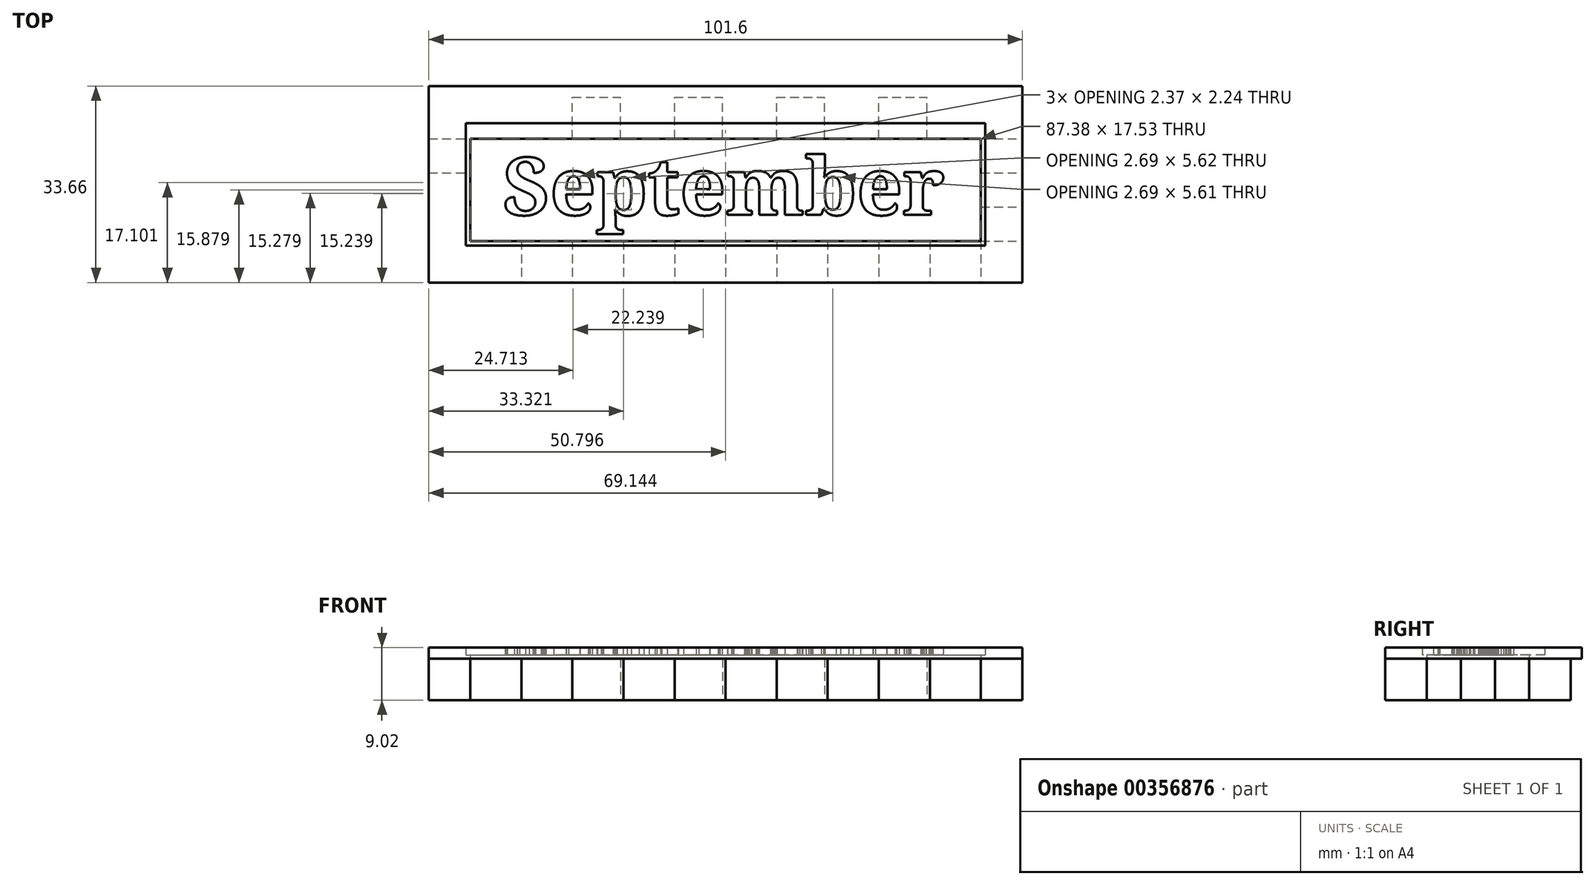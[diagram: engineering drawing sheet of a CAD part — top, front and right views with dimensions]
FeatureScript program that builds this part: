
annotation { "Feature Type Name" : "Feature", "Feature Type Description" : "" }
export const myFeature = defineFeature(function(context is Context, id is Id, definition is map)
    precondition{}
    {
        {
            var Q0;
            Q0=qCreatedBy(makeId("Top.planeOp"),FACE);
            var sketch = newSketch(context, id + "F0", { "sketchPlane" : qUnion([Q0])});
            skLineSegment(sketch, "E0.bottom", {"start": v(-52.12, 11.37) * mm, "end": v(49.48, 11.37) * mm});
            skLineSegment(sketch, "E0.top", {"start": v(-52.12, -20.38) * mm, "end": v(49.48, -20.38) * mm});
            skLineSegment(sketch, "E0.left", {"start": v(-52.12, 11.37) * mm, "end": v(-52.12, -20.38) * mm});
            skLineSegment(sketch, "E0.right", {"start": v(49.48, 11.37) * mm, "end": v(49.48, -20.38) * mm});
            skLineSegment(sketch, "E1.bottom", {"start": v(-52.12, 11.37) * mm, "end": v(-45.01, 11.37) * mm});
            skLineSegment(sketch, "E1.top", {"start": v(-52.12, 4.26) * mm, "end": v(-45.01, 4.26) * mm});
            skLineSegment(sketch, "E1.left", {"start": v(-52.12, 11.37) * mm, "end": v(-52.12, 4.26) * mm});
            skLineSegment(sketch, "E1.right", {"start": v(-45.01, 11.37) * mm, "end": v(-45.01, 4.26) * mm});
            skLineSegment(sketch, "E2.bottom", {"start": v(-45.01, 11.37) * mm, "end": v(-36.78, 11.37) * mm});
            skLineSegment(sketch, "E2.top", {"start": v(-45.01, 4.26) * mm, "end": v(-36.78, 4.26) * mm});
            skLineSegment(sketch, "E2.right", {"start": v(-36.78, 11.37) * mm, "end": v(-36.78, 4.26) * mm});
            skLineSegment(sketch, "E3.bottom", {"start": v(-36.78, 4.26) * mm, "end": v(-27.54, 4.26) * mm});
            skLineSegment(sketch, "E3.top", {"start": v(-36.78, 11.37) * mm, "end": v(-27.54, 11.37) * mm});
            skLineSegment(sketch, "E3.left", {"start": v(-36.78, 4.26) * mm, "end": v(-36.78, 11.37) * mm});
            skLineSegment(sketch, "E3.right", {"start": v(-27.54, 4.26) * mm, "end": v(-27.54, 11.37) * mm});
            skLineSegment(sketch, "E4.bottom", {"start": v(-27.54, 4.26) * mm, "end": v(-19.3, 4.26) * mm});
            skLineSegment(sketch, "E4.top", {"start": v(-27.54, 11.37) * mm, "end": v(-19.3, 11.37) * mm});
            skLineSegment(sketch, "E4.right", {"start": v(-19.3, 4.26) * mm, "end": v(-19.3, 11.37) * mm});
            skLineSegment(sketch, "E5.bottom", {"start": v(-19.3, 4.26) * mm, "end": v(-10.06, 4.26) * mm});
            skLineSegment(sketch, "E5.top", {"start": v(-19.3, 11.37) * mm, "end": v(-10.06, 11.37) * mm});
            skLineSegment(sketch, "E5.right", {"start": v(-10.06, 4.26) * mm, "end": v(-10.06, 11.37) * mm});
            skLineSegment(sketch, "E6.bottom", {"start": v(-10.06, 4.26) * mm, "end": v(-10.06, 4.26) * mm});
            skLineSegment(sketch, "E6.top", {"start": v(-10.06, 11.37) * mm, "end": v(-10.06, 11.37) * mm});
            skLineSegment(sketch, "E7.bottom", {"start": v(-10.06, 4.26) * mm, "end": v(-1.83, 4.26) * mm});
            skLineSegment(sketch, "E7.top", {"start": v(-10.06, 11.37) * mm, "end": v(-1.83, 11.37) * mm});
            skLineSegment(sketch, "E7.right", {"start": v(-1.83, 4.26) * mm, "end": v(-1.83, 11.37) * mm});
            skLineSegment(sketch, "E8.bottom", {"start": v(-1.83, 4.26) * mm, "end": v(7.41, 4.26) * mm});
            skLineSegment(sketch, "E8.top", {"start": v(-1.83, 11.37) * mm, "end": v(7.41, 11.37) * mm});
            skLineSegment(sketch, "E8.right", {"start": v(7.41, 4.26) * mm, "end": v(7.41, 11.37) * mm});
            skLineSegment(sketch, "E9.bottom", {"start": v(7.41, 4.26) * mm, "end": v(15.64, 4.26) * mm});
            skLineSegment(sketch, "E9.top", {"start": v(7.41, 11.37) * mm, "end": v(15.64, 11.37) * mm});
            skLineSegment(sketch, "E9.right", {"start": v(15.64, 4.26) * mm, "end": v(15.64, 11.37) * mm});
            skLineSegment(sketch, "E10.bottom", {"start": v(15.64, 4.26) * mm, "end": v(24.89, 4.26) * mm});
            skLineSegment(sketch, "E10.top", {"start": v(15.64, 11.37) * mm, "end": v(24.89, 11.37) * mm});
            skLineSegment(sketch, "E10.right", {"start": v(24.89, 4.26) * mm, "end": v(24.89, 11.37) * mm});
            skLineSegment(sketch, "E11.bottom", {"start": v(24.89, 4.26) * mm, "end": v(24.89, 4.26) * mm});
            skLineSegment(sketch, "E11.top", {"start": v(24.89, 11.37) * mm, "end": v(24.89, 11.37) * mm});
            skLineSegment(sketch, "E12.bottom", {"start": v(24.89, 4.26) * mm, "end": v(33.12, 4.26) * mm});
            skLineSegment(sketch, "E12.top", {"start": v(24.89, 11.37) * mm, "end": v(33.12, 11.37) * mm});
            skLineSegment(sketch, "E12.right", {"start": v(33.12, 4.26) * mm, "end": v(33.12, 11.37) * mm});
            skLineSegment(sketch, "E13.bottom", {"start": v(33.12, 4.26) * mm, "end": v(42.36, 4.26) * mm});
            skLineSegment(sketch, "E13.top", {"start": v(33.12, 11.37) * mm, "end": v(42.36, 11.37) * mm});
            skLineSegment(sketch, "E13.right", {"start": v(42.36, 4.26) * mm, "end": v(42.36, 11.37) * mm});
            skLineSegment(sketch, "E14.bottom", {"start": v(42.36, 4.26) * mm, "end": v(49.48, 4.26) * mm});
            skLineSegment(sketch, "E14.top", {"start": v(42.36, 11.37) * mm, "end": v(49.48, 11.37) * mm});
            skLineSegment(sketch, "E14.right", {"start": v(49.48, 4.26) * mm, "end": v(49.48, 11.37) * mm});
            skLineSegment(sketch, "E15.bottom", {"start": v(-52.12, -20.38) * mm, "end": v(-45.01, -20.38) * mm});
            skLineSegment(sketch, "E15.top", {"start": v(-52.12, -13.26) * mm, "end": v(-45.01, -13.26) * mm});
            skLineSegment(sketch, "E15.left", {"start": v(-52.12, -20.38) * mm, "end": v(-52.12, -13.26) * mm});
            skLineSegment(sketch, "E15.right", {"start": v(-45.01, -20.38) * mm, "end": v(-45.01, -13.26) * mm});
            skLineSegment(sketch, "E16.bottom", {"start": v(-45.01, -13.26) * mm, "end": v(-45.01, -13.26) * mm});
            skLineSegment(sketch, "E16.top", {"start": v(-45.01, -20.38) * mm, "end": v(-45.01, -20.38) * mm});
            skLineSegment(sketch, "E16.left", {"start": v(-45.01, -13.26) * mm, "end": v(-45.01, -20.38) * mm});
            skLineSegment(sketch, "E16.right", {"start": v(-45.01, -13.26) * mm, "end": v(-45.01, -20.38) * mm});
            skLineSegment(sketch, "E17.bottom", {"start": v(-45.01, -13.26) * mm, "end": v(-36.27, -13.26) * mm});
            skLineSegment(sketch, "E17.top", {"start": v(-45.01, -20.38) * mm, "end": v(-36.27, -20.38) * mm});
            skLineSegment(sketch, "E17.right", {"start": v(-36.27, -13.26) * mm, "end": v(-36.27, -20.38) * mm});
            skLineSegment(sketch, "E18.bottom", {"start": v(-36.27, -13.26) * mm, "end": v(-36.27, -13.26) * mm});
            skLineSegment(sketch, "E18.top", {"start": v(-36.27, -20.38) * mm, "end": v(-36.27, -20.38) * mm});
            skLineSegment(sketch, "E19.bottom", {"start": v(-36.27, -13.26) * mm, "end": v(-27.54, -13.26) * mm});
            skLineSegment(sketch, "E19.top", {"start": v(-36.27, -20.38) * mm, "end": v(-27.54, -20.38) * mm});
            skLineSegment(sketch, "E19.right", {"start": v(-27.54, -13.26) * mm, "end": v(-27.54, -20.38) * mm});
            skLineSegment(sketch, "E20.bottom", {"start": v(-27.54, -13.26) * mm, "end": v(-18.8, -13.26) * mm});
            skLineSegment(sketch, "E20.top", {"start": v(-27.54, -20.38) * mm, "end": v(-18.8, -20.38) * mm});
            skLineSegment(sketch, "E20.right", {"start": v(-18.8, -13.26) * mm, "end": v(-18.8, -20.38) * mm});
            skLineSegment(sketch, "E21.bottom", {"start": v(-18.8, -13.26) * mm, "end": v(-10.06, -13.26) * mm});
            skLineSegment(sketch, "E21.top", {"start": v(-18.8, -20.38) * mm, "end": v(-10.06, -20.38) * mm});
            skLineSegment(sketch, "E21.right", {"start": v(-10.06, -13.26) * mm, "end": v(-10.06, -20.38) * mm});
            skLineSegment(sketch, "E22.bottom", {"start": v(-10.06, -13.26) * mm, "end": v(-1.32, -13.26) * mm});
            skLineSegment(sketch, "E22.top", {"start": v(-10.06, -20.38) * mm, "end": v(-1.32, -20.38) * mm});
            skLineSegment(sketch, "E22.right", {"start": v(-1.32, -13.26) * mm, "end": v(-1.32, -20.38) * mm});
            skLineSegment(sketch, "E23.bottom", {"start": v(-1.32, -13.26) * mm, "end": v(7.41, -13.26) * mm});
            skLineSegment(sketch, "E23.top", {"start": v(-1.32, -20.38) * mm, "end": v(7.41, -20.38) * mm});
            skLineSegment(sketch, "E23.right", {"start": v(7.41, -13.26) * mm, "end": v(7.41, -20.38) * mm});
            skLineSegment(sketch, "E24.bottom", {"start": v(7.41, -13.26) * mm, "end": v(16.15, -13.26) * mm});
            skLineSegment(sketch, "E24.top", {"start": v(7.41, -20.38) * mm, "end": v(16.15, -20.38) * mm});
            skLineSegment(sketch, "E24.right", {"start": v(16.15, -13.26) * mm, "end": v(16.15, -20.38) * mm});
            skLineSegment(sketch, "E25.bottom", {"start": v(16.15, -13.26) * mm, "end": v(24.89, -13.26) * mm});
            skLineSegment(sketch, "E25.top", {"start": v(16.15, -20.38) * mm, "end": v(24.89, -20.38) * mm});
            skLineSegment(sketch, "E25.right", {"start": v(24.89, -13.26) * mm, "end": v(24.89, -20.38) * mm});
            skLineSegment(sketch, "E26.bottom", {"start": v(24.89, -13.26) * mm, "end": v(33.63, -13.26) * mm});
            skLineSegment(sketch, "E26.top", {"start": v(24.89, -20.38) * mm, "end": v(33.63, -20.38) * mm});
            skLineSegment(sketch, "E26.right", {"start": v(33.63, -13.26) * mm, "end": v(33.63, -20.38) * mm});
            skLineSegment(sketch, "E27.bottom", {"start": v(33.63, -13.26) * mm, "end": v(42.36, -13.26) * mm});
            skLineSegment(sketch, "E27.top", {"start": v(33.63, -20.38) * mm, "end": v(42.36, -20.38) * mm});
            skLineSegment(sketch, "E27.right", {"start": v(42.36, -13.26) * mm, "end": v(42.36, -20.38) * mm});
            skLineSegment(sketch, "E28.bottom", {"start": v(42.36, -13.26) * mm, "end": v(49.48, -13.26) * mm});
            skLineSegment(sketch, "E28.top", {"start": v(42.36, -20.38) * mm, "end": v(49.48, -20.38) * mm});
            skLineSegment(sketch, "E28.right", {"start": v(49.48, -13.26) * mm, "end": v(49.48, -20.38) * mm});
            skLineSegment(sketch, "E29.top", {"start": v(-52.12, -1.58) * mm, "end": v(-45.01, -1.58) * mm});
            skLineSegment(sketch, "E29.left", {"start": v(-52.12, 4.26) * mm, "end": v(-52.12, -1.58) * mm});
            skLineSegment(sketch, "E29.right", {"start": v(-45.01, 4.26) * mm, "end": v(-45.01, -1.58) * mm});
            skLineSegment(sketch, "E30.top", {"start": v(-52.12, -7.42) * mm, "end": v(-45.01, -7.42) * mm});
            skLineSegment(sketch, "E30.left", {"start": v(-52.12, -1.58) * mm, "end": v(-52.12, -7.42) * mm});
            skLineSegment(sketch, "E30.right", {"start": v(-45.01, -1.58) * mm, "end": v(-45.01, -7.42) * mm});
            skLineSegment(sketch, "E31.bottom", {"start": v(-45.01, -7.42) * mm, "end": v(-52.12, -7.42) * mm});
            skLineSegment(sketch, "E31.top", {"start": v(-45.01, -13.26) * mm, "end": v(-52.12, -13.26) * mm});
            skLineSegment(sketch, "E31.left", {"start": v(-45.01, -7.42) * mm, "end": v(-45.01, -13.26) * mm});
            skLineSegment(sketch, "E31.right", {"start": v(-52.12, -7.42) * mm, "end": v(-52.12, -13.26) * mm});
            skLineSegment(sketch, "E32.top", {"start": v(42.36, -1.58) * mm, "end": v(49.48, -1.58) * mm});
            skLineSegment(sketch, "E32.left", {"start": v(42.36, 4.26) * mm, "end": v(42.36, -1.58) * mm});
            skLineSegment(sketch, "E32.right", {"start": v(49.48, 4.26) * mm, "end": v(49.48, -1.58) * mm});
            skLineSegment(sketch, "E33.top", {"start": v(42.36, -7.42) * mm, "end": v(49.48, -7.42) * mm});
            skLineSegment(sketch, "E33.left", {"start": v(42.36, -1.58) * mm, "end": v(42.36, -7.42) * mm});
            skLineSegment(sketch, "E33.right", {"start": v(49.48, -1.58) * mm, "end": v(49.48, -7.42) * mm});
            skLineSegment(sketch, "E34.left", {"start": v(42.36, -7.42) * mm, "end": v(42.36, -13.26) * mm});
            skLineSegment(sketch, "E34.right", {"start": v(49.48, -7.42) * mm, "end": v(49.48, -13.26) * mm});
            skSolve(sketch);
        }
        {
            var Q0;
            Q0=makeQuery(id+"F0.imprint","IMPRINT",FACE,{"disambiguationData":[TD([[makeQuery(id+"F0.imprint","IMPRINT",EDGE,{"derivedFrom":sQuery(id+"F0.wireOp",EDGE,"E2.top")}),-1.0]])]});
            var Q1;
            Q1=makeQuery(id+"F0.imprint","IMPRINT",FACE,{"disambiguationData":[TD([[makeQuery(id+"F0.imprint","IMPRINT",EDGE,{"derivedFrom":sQuery(id+"F0.wireOp",EDGE,"E2.bottom")}),-1.0]])]});
            var Q2;
            Q2=makeQuery(id+"F0.imprint","IMPRINT",FACE,{"disambiguationData":[TD([[makeQuery(id+"F0.imprint","IMPRINT",EDGE,{"derivedFrom":sQuery(id+"F0.wireOp",EDGE,"E4.bottom")}),1.0]])]});
            var Q3;
            Q3=makeQuery(id+"F0.imprint","IMPRINT",FACE,{"disambiguationData":[TD([[makeQuery(id+"F0.imprint","IMPRINT",EDGE,{"derivedFrom":sQuery(id+"F0.wireOp",EDGE,"E7.bottom")}),1.0]])]});
            var Q4;
            Q4=makeQuery(id+"F0.imprint","IMPRINT",FACE,{"disambiguationData":[TD([[makeQuery(id+"F0.imprint","IMPRINT",EDGE,{"derivedFrom":sQuery(id+"F0.wireOp",EDGE,"E9.bottom")}),1.0]])]});
            var Q5;
            Q5=makeQuery(id+"F0.imprint","IMPRINT",FACE,{"disambiguationData":[TD([[makeQuery(id+"F0.imprint","IMPRINT",EDGE,{"derivedFrom":sQuery(id+"F0.wireOp",EDGE,"E12.bottom")}),1.0]])]});
            var Q6;
            Q6=makeQuery(id+"F0.imprint","IMPRINT",FACE,{"disambiguationData":[TD([[makeQuery(id+"F0.imprint","IMPRINT",EDGE,{"derivedFrom":sQuery(id+"F0.wireOp",EDGE,"E14.bottom")}),-1.0]])]});
            var Q7;
            Q7=makeQuery(id+"F0.imprint","IMPRINT",FACE,{"disambiguationData":[TD([[makeQuery(id+"F0.imprint","IMPRINT",EDGE,{"derivedFrom":sQuery(id+"F0.wireOp",EDGE,"E33.top")}),-1.0]])]});
            var Q8;
            Q8=makeQuery(id+"F0.imprint","IMPRINT",FACE,{"disambiguationData":[TD([[makeQuery(id+"F0.imprint","IMPRINT",EDGE,{"derivedFrom":sQuery(id+"F0.wireOp",EDGE,"E27.bottom")}),-1.0]])]});
            var Q9;
            Q9=makeQuery(id+"F0.imprint","IMPRINT",FACE,{"disambiguationData":[TD([[makeQuery(id+"F0.imprint","IMPRINT",EDGE,{"derivedFrom":sQuery(id+"F0.wireOp",EDGE,"E25.bottom")}),-1.0]])]});
            var Q10;
            Q10=makeQuery(id+"F0.imprint","IMPRINT",FACE,{"disambiguationData":[TD([[makeQuery(id+"F0.imprint","IMPRINT",EDGE,{"derivedFrom":sQuery(id+"F0.wireOp",EDGE,"E23.bottom")}),-1.0]])]});
            var Q11;
            Q11=makeQuery(id+"F0.imprint","IMPRINT",FACE,{"disambiguationData":[TD([[makeQuery(id+"F0.imprint","IMPRINT",EDGE,{"derivedFrom":sQuery(id+"F0.wireOp",EDGE,"E21.bottom")}),-1.0]])]});
            var Q12;
            Q12=makeQuery(id+"F0.imprint","IMPRINT",FACE,{"disambiguationData":[TD([[makeQuery(id+"F0.imprint","IMPRINT",EDGE,{"derivedFrom":sQuery(id+"F0.wireOp",EDGE,"E19.bottom")}),-1.0]])]});
            var Q13;
            Q13=makeQuery(id+"F0.imprint","IMPRINT",FACE,{"disambiguationData":[TD([[makeQuery(id+"F0.imprint","IMPRINT",EDGE,{"derivedFrom":sQuery(id+"F0.wireOp",EDGE,"E31.bottom")}),1.0]])]});
            var Q14;
            Q14=makeQuery(id+"F0.imprint","IMPRINT",FACE,{"disambiguationData":[TD([[makeQuery(id+"F0.imprint","IMPRINT",EDGE,{"derivedFrom":sQuery(id+"F0.wireOp",EDGE,"E1.top")}),-1.0]])]});
            extrude(context, id + "F1", {"entities" : qUnion([Q0, Q1, Q2, Q3, Q4, Q5, Q6, Q7, Q8, Q9, Q10, Q11, Q12, Q13, Q14]), "depth" : 7.11 * mm});
        }
        {
            var Q0;
            Q0=makeQuery(id+"F1.opExtrude","CAP_FACE",FACE,{"disambiguationData":[OSD([sQuery(id+"F0.wireOp",EDGE,"E2.bottom"),sQuery(id+"F0.wireOp",EDGE,"E1.right"),sQuery(id+"F0.wireOp",EDGE,"E3.bottom"),sQuery(id+"F0.wireOp",EDGE,"E3.left"),sQuery(id+"F0.wireOp",EDGE,"E4.top"),sQuery(id+"F0.wireOp",EDGE,"E3.right"),sQuery(id+"F0.wireOp",EDGE,"E5.bottom"),sQuery(id+"F0.wireOp",EDGE,"E4.right"),sQuery(id+"F0.wireOp",EDGE,"E6.top"),sQuery(id+"F0.wireOp",EDGE,"E5.right"),sQuery(id+"F0.wireOp",EDGE,"E7.bottom"),sQuery(id+"F0.wireOp",EDGE,"E5.right"),sQuery(id+"F0.wireOp",EDGE,"E8.top"),sQuery(id+"F0.wireOp",EDGE,"E7.right"),sQuery(id+"F0.wireOp",EDGE,"E9.bottom"),sQuery(id+"F0.wireOp",EDGE,"E8.right"),sQuery(id+"F0.wireOp",EDGE,"E10.top"),sQuery(id+"F0.wireOp",EDGE,"E9.right"),sQuery(id+"F0.wireOp",EDGE,"E11.bottom"),sQuery(id+"F0.wireOp",EDGE,"E10.right"),sQuery(id+"F0.wireOp",EDGE,"E12.top"),sQuery(id+"F0.wireOp",EDGE,"E10.right"),sQuery(id+"F0.wireOp",EDGE,"E13.bottom"),sQuery(id+"F0.wireOp",EDGE,"E12.right"),sQuery(id+"F0.wireOp",EDGE,"E16.bottom"),sQuery(id+"F0.wireOp",EDGE,"E17.top"),sQuery(id+"F0.wireOp",EDGE,"E16.left"),sQuery(id+"F0.wireOp",EDGE,"E18.bottom"),sQuery(id+"F0.wireOp",EDGE,"E17.right"),sQuery(id+"F0.wireOp",EDGE,"E19.top"),sQuery(id+"F0.wireOp",EDGE,"E17.right"),sQuery(id+"F0.wireOp",EDGE,"E20.bottom"),sQuery(id+"F0.wireOp",EDGE,"E19.right"),sQuery(id+"F0.wireOp",EDGE,"E21.top"),sQuery(id+"F0.wireOp",EDGE,"E20.right"),sQuery(id+"F0.wireOp",EDGE,"E22.bottom"),sQuery(id+"F0.wireOp",EDGE,"E21.right"),sQuery(id+"F0.wireOp",EDGE,"E23.top"),sQuery(id+"F0.wireOp",EDGE,"E22.right"),sQuery(id+"F0.wireOp",EDGE,"E24.bottom"),sQuery(id+"F0.wireOp",EDGE,"E23.right"),sQuery(id+"F0.wireOp",EDGE,"E25.top"),sQuery(id+"F0.wireOp",EDGE,"E24.right"),sQuery(id+"F0.wireOp",EDGE,"E26.bottom"),sQuery(id+"F0.wireOp",EDGE,"E25.right"),sQuery(id+"F0.wireOp",EDGE,"E27.top"),sQuery(id+"F0.wireOp",EDGE,"E26.right"),sQuery(id+"F0.wireOp",EDGE,"E27.right"),sQuery(id+"F0.wireOp",EDGE,"E1.top"),sQuery(id+"F0.wireOp",EDGE,"E29.left"),sQuery(id+"F0.wireOp",EDGE,"E29.top"),sQuery(id+"F0.wireOp",EDGE,"E30.right"),sQuery(id+"F0.wireOp",EDGE,"E31.bottom"),sQuery(id+"F0.wireOp",EDGE,"E31.top"),sQuery(id+"F0.wireOp",EDGE,"E31.right"),sQuery(id+"F0.wireOp",EDGE,"E14.bottom"),sQuery(id+"F0.wireOp",EDGE,"E32.right"),sQuery(id+"F0.wireOp",EDGE,"E32.top"),sQuery(id+"F0.wireOp",EDGE,"E33.left"),sQuery(id+"F0.wireOp",EDGE,"E33.top"),sQuery(id+"F0.wireOp",EDGE,"E28.bottom"),sQuery(id+"F0.wireOp",EDGE,"E34.right")])],"isStart":false});
            var sketch = newSketch(context, id + "F2", { "sketchPlane" : qUnion([Q0])});
            skLineSegment(sketch, "E35.bottom", {"start": v(-52.12, -20.38) * mm, "end": v(-45.01, -20.38) * mm});
            skLineSegment(sketch, "E35.top", {"start": v(-52.12, 13.28) * mm, "end": v(-45.01, 13.28) * mm});
            skLineSegment(sketch, "E35.left", {"start": v(-52.12, -20.38) * mm, "end": v(-52.12, 13.28) * mm});
            skLineSegment(sketch, "E35.right", {"start": v(-45.01, -20.38) * mm, "end": v(-45.01, 13.28) * mm});
            skLineSegment(sketch, "E36.bottom", {"start": v(-52.12, -20.38) * mm, "end": v(49.48, -20.38) * mm});
            skLineSegment(sketch, "E36.top", {"start": v(-52.12, -13.26) * mm, "end": v(49.48, -13.26) * mm});
            skLineSegment(sketch, "E36.left", {"start": v(-52.12, -20.38) * mm, "end": v(-52.12, -13.26) * mm});
            skLineSegment(sketch, "E36.right", {"start": v(49.48, -20.38) * mm, "end": v(49.48, -13.26) * mm});
            skPoint(sketch, "E37.oppositeSnap0", {"position": v(42.36, -4.5) * mm});
            skLineSegment(sketch, "E37.bottom", {"start": v(49.48, -20.38) * mm, "end": v(42.36, -20.38) * mm});
            skLineSegment(sketch, "E37.top", {"start": v(49.48, 13.28) * mm, "end": v(42.36, 13.28) * mm});
            skLineSegment(sketch, "E37.left", {"start": v(49.48, -20.38) * mm, "end": v(49.48, 13.28) * mm});
            skLineSegment(sketch, "E37.right", {"start": v(42.36, -20.38) * mm, "end": v(42.36, 13.28) * mm});
            skLineSegment(sketch, "E38.bottom", {"start": v(-52.12, 13.28) * mm, "end": v(49.48, 13.28) * mm});
            skLineSegment(sketch, "E38.top", {"start": v(-52.12, 4.26) * mm, "end": v(49.48, 4.26) * mm});
            skLineSegment(sketch, "E38.left", {"start": v(-52.12, 13.28) * mm, "end": v(-52.12, 4.26) * mm});
            skLineSegment(sketch, "E38.right", {"start": v(49.48, 13.28) * mm, "end": v(49.48, 4.26) * mm});
            skSolve(sketch);
        }
        {
            var Q0;
            Q0=qSketchRegion(id+"F2",true);
            var Q1;
            {var subQ5=sQuery(id+"F2.wireOp",EDGE,"E36.top");var subQ10=sQuery(id+"F2.wireOp",EDGE,"E35.right");var subQ12=makeQuery(id+"F2.imprint","INTERSECT",VERTEX,{"derivedFrom":[makeQuery(id+"F1.opExtrude","CAP_EDGE",EDGE,{"disambiguationData":[OSD([sQuery(id+"F0.wireOp",EDGE,"E31.bottom")])],"isStart":false}),subQ10]});var subQ24=makeQuery(id+"F2.imprint","INTERSECT",VERTEX,{"derivedFrom":[subQ10,subQ5]});Q1=makeQuery(id+"F2.imprint","IMPRINT",FACE,{"disambiguationData":[TD([[makeQuery(id+"F2.imprint","IMPRINT",EDGE,{"disambiguationData":[TD([[subQ12,1.0],[subQ24,-1.0]])],"derivedFrom":subQ10}),-1.0]])]});}
            extrude(context, id + "F3", {"entities" : qUnion([Q0, Q1]), "depth" : 0.64 * mm});
        }
        {
            var Q0;
            Q0=makeQuery(id+"F3.opExtrude","CAP_FACE",FACE,{"disambiguationData":[OSD([sQuery(id+"F2.wireOp",EDGE,"E35.left"),sQuery(id+"F2.wireOp",EDGE,"E36.bottom"),sQuery(id+"F2.wireOp",EDGE,"E36.left"),sQuery(id+"F2.wireOp",EDGE,"E37.bottom"),sQuery(id+"F2.wireOp",EDGE,"E37.left"),sQuery(id+"F2.wireOp",EDGE,"E38.bottom"),sQuery(id+"F2.wireOp",EDGE,"E38.left"),sQuery(id+"F2.wireOp",EDGE,"E38.right")])],"isStart":false});
            var sketch = newSketch(context, id + "F4", { "sketchPlane" : qUnion([Q0])});
            skLineSegment(sketch, "E39.bottom", {"start": v(-52.12, 13.28) * mm, "end": v(49.48, 13.28) * mm});
            skLineSegment(sketch, "E39.top", {"start": v(-52.12, 6.93) * mm, "end": v(49.48, 6.93) * mm});
            skLineSegment(sketch, "E39.left", {"start": v(-52.12, 13.28) * mm, "end": v(-52.12, 6.93) * mm});
            skLineSegment(sketch, "E39.right", {"start": v(49.48, 13.28) * mm, "end": v(49.48, 6.93) * mm});
            skLineSegment(sketch, "E40.bottom", {"start": v(-52.12, 13.28) * mm, "end": v(-45.77, 13.28) * mm});
            skLineSegment(sketch, "E40.top", {"start": v(-52.12, -20.38) * mm, "end": v(-45.77, -20.38) * mm});
            skLineSegment(sketch, "E40.left", {"start": v(-52.12, 13.28) * mm, "end": v(-52.12, -20.38) * mm});
            skLineSegment(sketch, "E40.right", {"start": v(-45.77, 13.28) * mm, "end": v(-45.77, -20.38) * mm});
            skLineSegment(sketch, "E41.bottom", {"start": v(-52.12, -14.03) * mm, "end": v(49.48, -14.03) * mm});
            skLineSegment(sketch, "E41.top", {"start": v(-52.12, -20.38) * mm, "end": v(49.48, -20.38) * mm});
            skLineSegment(sketch, "E41.left", {"start": v(-52.12, -14.03) * mm, "end": v(-52.12, -20.38) * mm});
            skLineSegment(sketch, "E41.right", {"start": v(49.48, -14.03) * mm, "end": v(49.48, -20.38) * mm});
            skLineSegment(sketch, "E42.bottom", {"start": v(49.48, -20.38) * mm, "end": v(43.13, -20.38) * mm});
            skLineSegment(sketch, "E42.top", {"start": v(49.48, 13.28) * mm, "end": v(43.13, 13.28) * mm});
            skLineSegment(sketch, "E42.left", {"start": v(49.48, -20.38) * mm, "end": v(49.48, 13.28) * mm});
            skLineSegment(sketch, "E42.right", {"start": v(43.13, -20.38) * mm, "end": v(43.13, 13.28) * mm});
            skSolve(sketch);
        }
        {
            var Q0;
            Q0=qSketchRegion(id+"F4",true);
            extrude(context, id + "F5", {"entities" : qUnion([Q0]), "operationType" : NewBodyOperationType.ADD, "depth" : 1.27 * mm});
        }
        {
            var Q0;
            Q0=makeQuery(id+"F3.opExtrude","CAP_FACE",FACE,{"disambiguationData":[OSD([sQuery(id+"F2.wireOp",EDGE,"E35.left"),sQuery(id+"F2.wireOp",EDGE,"E36.bottom"),sQuery(id+"F2.wireOp",EDGE,"E36.left"),sQuery(id+"F2.wireOp",EDGE,"E37.bottom"),sQuery(id+"F2.wireOp",EDGE,"E37.left"),sQuery(id+"F2.wireOp",EDGE,"E38.bottom"),sQuery(id+"F2.wireOp",EDGE,"E38.left"),sQuery(id+"F2.wireOp",EDGE,"E38.right")])],"isStart":false});
            var sketch = newSketch(context, id + "F6", { "sketchPlane" : qUnion([Q0])});
            skText(sketch, "E43", { "text": "September", "fontName": "NotoSerif-Bold.ttf"});
            const initialGuessF6  = {"E43": [-0.03942, -0.0088, 1, 0, 0.00988]};
            skSetInitialGuess(sketch, initialGuessF6);
            skSolve(sketch);
        }
        {
            var Q0;
            Q0 = qSketchRegion(id + "F6", true);
            extrude(context, id + "F7", {"entities" : qUnion([Q0]), "operationType" : NewBodyOperationType.ADD, "depth" : 1.27 * mm});
        }
    });
